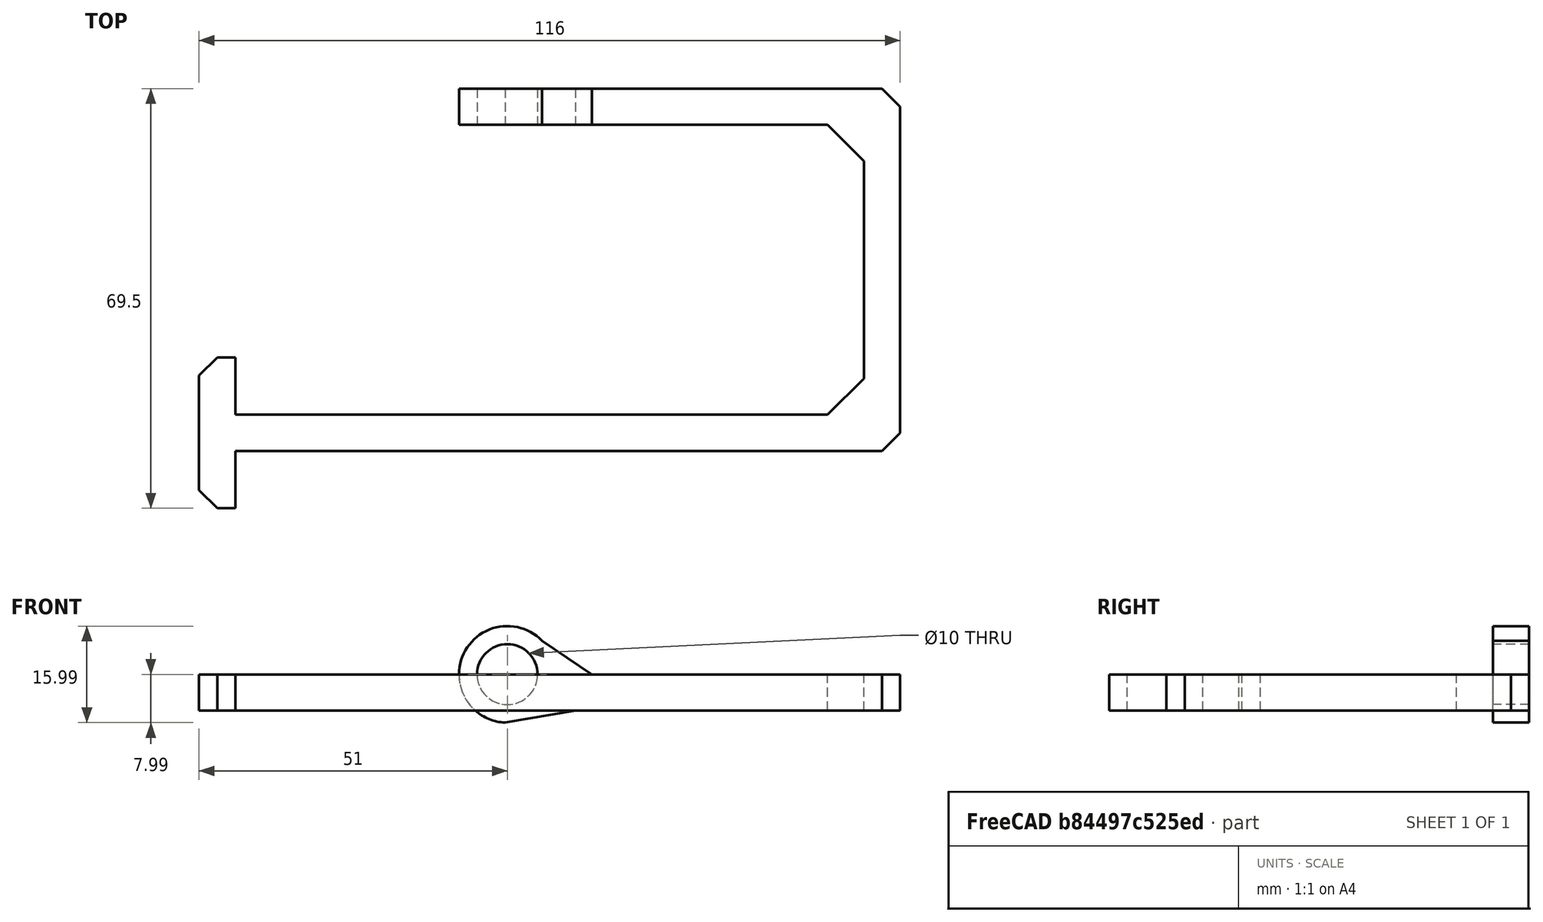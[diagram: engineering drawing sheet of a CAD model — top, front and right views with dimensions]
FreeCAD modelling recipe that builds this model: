
FCSTD DOCUMENT  (FreeCAD 0.19R24276 (Git))
Label: porta_rollos
License: All rights reserved
LicenseURL: http://en.wikipedia.org/wiki/All_rights_reserved
objects: TechDraw::DrawViewDimension×16, Part::Chamfer×8, TechDraw::DrawProjGroupItem×3, Part::Cylinder×2, TechDraw::DrawSVGTemplate×2, TechDraw::DrawViewPart×2, TechDraw::DrawPage×2, Sketcher::SketchObject×1, PartDesign::Pad×1, Part::Cut×1, Part::MultiFuse×1, TechDraw::DrawProjGroup×1, TechDraw::DrawViewAnnotation×1
note: 15 computed .brp shape members not serialized (recipe doc carries the construction recipe); baked Part::Feature solids carry a one-line shape summary decoded from their .brp

FEATURE [Sketcher::SketchObject] Sketch
  FullyConstrained = false
  MapMode = 5
  sketch-geometry (15):
    g0: LineSegment StartX=8 StartY=3 StartZ=0 EndX=68 EndY=3 EndZ=0
    g1: LineSegment StartX=68 StartY=3 StartZ=0 EndX=68 EndY=-57 EndZ=0
    g2: LineSegment StartX=68 StartY=-57 StartZ=0 EndX=-42 EndY=-57 EndZ=0
    g3: LineSegment StartX=-42 StartY=-51 StartZ=0 EndX=62 EndY=-51 EndZ=0
    g4: LineSegment StartX=62 StartY=-51 StartZ=0 EndX=62 EndY=-3 EndZ=0
    g5: LineSegment StartX=62 StartY=-3 StartZ=0 EndX=8 EndY=-3 EndZ=0
    g6: LineSegment StartX=8 StartY=3 StartZ=0 EndX=8 EndY=-3 EndZ=0
    g7: LineSegment StartX=62 StartY=-51 StartZ=0 EndX=68 EndY=-51 EndZ=0
    g8: LineSegment StartX=0 StartY=0 StartZ=0 EndX=8 EndY=0 EndZ=0
    g9: LineSegment StartX=-42 StartY=-51 StartZ=0 EndX=-42 EndY=-41.5 EndZ=0
    g10: LineSegment StartX=-42 StartY=-41.5 StartZ=0 EndX=-48 EndY=-41.5 EndZ=0
    g11: LineSegment StartX=-48 StartY=-41.5 StartZ=0 EndX=-48 EndY=-66.5 EndZ=0
    g12: LineSegment StartX=-48 StartY=-66.5 StartZ=0 EndX=-42 EndY=-66.5 EndZ=0
    g13: LineSegment StartX=-42 StartY=-66.5 StartZ=0 EndX=-42 EndY=-57 EndZ=0
    g14: LineSegment StartX=-42 StartY=-51 StartZ=0 EndX=-42 EndY=-57 EndZ=0
  constraints (43):
    c: Coincident(g1,g2)
    c: Coincident(g3,g4)
    c: Coincident(g4,g5)
    c: Vertical(g6)
    c: Horizontal(g0)
    c: Horizontal(g5)
    c: Horizontal(g3)
    c: Horizontal(g2)
    c: Vertical(g4)
    c: Vertical(g1)
    c: DistanceY(g6,g6) = 6
    c: Coincident(g1,g0)
    c: Horizontal(g7)
    c: Perpendicular(g7,g1) = 4.71239
    c: DistanceX(g7,g7) = 6
    c: DistanceX(g6,g0) = 60
    c: DistanceY(g1,g1) = 60
    c: DistanceX(g2,g2) = 110
    c: DistanceY(g2,g3) = 6
    c: Coincident(g7,g3)
    c: Coincident(g0,g6)
    c: Coincident(g5,g6)
    c: DistanceX(g8,g8) = 8
    c: Coincident(g8,g-1)
    c: Symmetric(g0,g5,g8)
    c: Perpendicular(g8,g6) = 4.71239
    c: Coincident(g9,g10)
    c: Coincident(g10,g11)
    c: Coincident(g11,g12)
    c: Coincident(g12,g13)
    c: Coincident(g13,g2)
    c: Coincident(g9,g3)
    c: Vertical(g9)
    c: Vertical(g13)
    c: Vertical(g11)
    c: Horizontal(g10)
    c: Horizontal(g12)
    c: Vertical(g14)
    c: Coincident(g14,g2)
    c: Coincident(g14,g3)
    c: DistanceX(g10,g10) = 6
    c: DistanceY(g11,g11) = 25
    c: DistanceY(g9,g9) = 9.5
FEATURE [PartDesign::Pad] Pad
  AllowMultiFace = false
  Direction = (1,1,1)
  Length = 6
  Length2 = 100
  Profile = -> Sketch
  Type = 0
FEATURE [Part::Cylinder] Cylinder  label="Cilindro"
  Angle = 360
  AttacherType = Attacher::AttachEngine3D
  Height = 6
  Placement = pos=(3,3,0) rot=(0,0,1;0rad)
  Radius = 8
FEATURE [Part::Cylinder] Cylinder001  label="Cilindro001"
  Angle = 360
  AttacherType = Attacher::AttachEngine3D
  Height = 6
  Placement = pos=(3,3,0) rot=(0,0,1;0rad)
  Radius = 5
FEATURE [Part::Cut] Cut
  Base = -> Cylinder
  Placement = pos=(0,3,3) rot=(1,0,0;1.5708rad)
  Tool = -> Cylinder001
FEATURE [Part::MultiFuse] Fusion
  Shapes = -> [Cut,Pad]
FEATURE [Part::Chamfer] Chamfer
  Base = -> Fusion
  Edges = 1 edges r=6: [Edge27]
FEATURE [Part::Chamfer] Chamfer001
  Base = -> Chamfer
  Edges = 1 edges r=6: [Edge41]
FEATURE [Part::Chamfer] Chamfer002
  Base = -> Chamfer001
  Edges = 1 edges r=6: [Edge40]
FEATURE [Part::Chamfer] Chamfer003
  Base = -> Chamfer002
  Edges = 1 edges r=6: [Edge15]
FEATURE [Part::Chamfer] Chamfer004
  Base = -> Chamfer003
  Edges = 1 edges r=3: [Edge36]
FEATURE [Part::Chamfer] Chamfer005
  Base = -> Chamfer004
  Edges = 1 edges r=3: [Edge26]
FEATURE [Part::Chamfer] Chamfer006
  Base = -> Chamfer005
  Edges = 1 edges r=3: [Edge35]
FEATURE [Part::Chamfer] Chamfer007
  Base = -> Chamfer006
  Edges = 1 edges r=3: [Edge25]
FEATURE [TechDraw::DrawSVGTemplate] Template
  EditableTexts = Designed_by_Name=<owner>; Drawing_number=001; FC-Date=-; FC-SC=1:3; FC-SH=1/2; FC-Title=Toilet Paper Holder; Subtitle=Porta Rollos Baño; Weight=<100gr
  Height = 210
  Orientation = 1
  Width = 297
FEATURE [TechDraw::DrawViewPart] View
  CoarseView = false
  Direction = (0.577,-0.577,0.577)
  Focus = 100
  HardHidden = false
  IsoCount = 0
  IsoHidden = false
  IsoVisible = false
  LockPosition = false
  Perspective = false
  Rotation = 0
  ScaleType = 0
  SeamHidden = false
  SeamVisible = true
  SmoothHidden = false
  SmoothVisible = true
  Source = -> [Chamfer007]
  X = 211.957
  XDirection = (0.707,0.707,0)
  Y = 129.533
FEATURE [TechDraw::DrawProjGroupItem] ProjItem  label="Front"
  CoarseView = false
  Direction = (0,-1,0)
  Focus = 100
  HardHidden = false
  IsoCount = 0
  IsoHidden = false
  IsoVisible = false
  LockPosition = true
  Perspective = false
  Rotation = 0
  RotationVector = (1,0,0)
  Scale = 0.5
  ScaleType = 2
  SeamHidden = false
  SeamVisible = true
  SmoothHidden = false
  SmoothVisible = true
  Source = -> [Chamfer007]
  Type = 0
  X = 0
  XDirection = (1,0,0)
  Y = 0
FEATURE [TechDraw::DrawProjGroupItem] ProjItem001  label="Right"
  CoarseView = false
  Direction = (1,-1e-16,0)
  Focus = 100
  HardHidden = false
  IsoCount = 0
  IsoHidden = false
  IsoVisible = false
  LockPosition = false
  Perspective = false
  Rotation = 0
  RotationVector = (1,0,0)
  ScaleType = 2
  SeamHidden = false
  SeamVisible = true
  SmoothHidden = false
  SmoothVisible = true
  Source = -> [Chamfer007]
  Type = 2
  X = -61.375
  XDirection = (1e-16,1,0)
  Y = 0
FEATURE [TechDraw::DrawProjGroupItem] ProjItem002  label="Top"
  CoarseView = false
  Direction = (0,0,1)
  Focus = 100
  HardHidden = false
  IsoCount = 0
  IsoHidden = false
  IsoVisible = false
  LockPosition = false
  Perspective = false
  Rotation = 0
  RotationVector = (1,0,0)
  ScaleType = 2
  SeamHidden = false
  SeamVisible = true
  SmoothHidden = false
  SmoothVisible = true
  Source = -> [Chamfer007]
  Type = 4
  X = 0
  XDirection = (1,0,0)
  Y = -49.75
FEATURE [TechDraw::DrawProjGroup] ProjGroup
  Anchor = -> ProjItem
  AutoDistribute = true
  LockPosition = false
  ProjectionType = 0
  Rotation = 0
  Scale = 0.5
  ScaleType = 2
  Source = -> [Chamfer007]
  Views = -> [ProjItem,ProjItem001,ProjItem002]
  X = 100.171
  Y = 156.257
  spacingX = 15
  spacingY = 15
FEATURE [TechDraw::DrawViewDimension] Dimension
  Arbitrary = false
  ArbitraryTolerances = false
  EqualTolerance = true
  FormatSpec = %.2f
  FormatSpecOverTolerance = %+.2f
  FormatSpecUnderTolerance = %+.2f
  Inverted = false
  LockPosition = false
  MeasureType = 1
  OverTolerance = 0
  References2D = -> [ProjItem002]
  Rotation = 0
  ScaleType = 0
  TheoreticalExact = false
  Type = 1
  UnderTolerance = 0
  X = -2.07471
  Y = 31.7463
FEATURE [TechDraw::DrawViewDimension] Dimension003
  Arbitrary = false
  ArbitraryTolerances = false
  EqualTolerance = true
  FormatSpec = %.2f
  FormatSpecOverTolerance = %+.2f
  FormatSpecUnderTolerance = %+.2f
  Inverted = false
  LockPosition = false
  MeasureType = 1
  OverTolerance = 0
  References2D = -> [ProjItem002]
  Rotation = 0
  ScaleType = 0
  TheoreticalExact = false
  Type = 2
  UnderTolerance = 0
  X = -47.3746
  Y = 3.19414
FEATURE [TechDraw::DrawPage] Page  label="Vistas"
  KeepUpdated = true
  NextBalloonIndex = 1
  ProjectionType = 0
  Template = -> Template
  Views = -> [View,ProjGroup,Dimension,Dimension003]
FEATURE [TechDraw::DrawSVGTemplate] Template001
  EditableTexts = Designed_by_Name=<owner>; Drawing_number=002; FC-Date=-; FC-SC=1:1; FC-SH=2/2; FC-Title=Toilet Paper Holder; Subtitle=Porta Rollos Baño; Weight=<100gr
  Height = 210
  Orientation = 1
  Width = 297
FEATURE [TechDraw::DrawViewPart] View001
  CoarseView = false
  Direction = (0.577,-0.577,0.577)
  Focus = 100
  HardHidden = false
  IsoCount = 0
  IsoHidden = false
  IsoVisible = false
  LockPosition = false
  Perspective = false
  Rotation = 0
  ScaleType = 0
  SeamHidden = false
  SeamVisible = true
  SmoothHidden = false
  SmoothVisible = true
  Source = -> [Chamfer007]
  X = 150.485
  XDirection = (0.707,0.707,0)
  Y = 127.165
FEATURE [TechDraw::DrawViewDimension] Dimension004
  Arbitrary = false
  ArbitraryTolerances = false
  EqualTolerance = true
  FormatSpec = %.2f
  FormatSpecOverTolerance = %+.2f
  FormatSpecUnderTolerance = %+.2f
  Inverted = false
  LockPosition = false
  MeasureType = 1
  OverTolerance = 0
  References2D = -> [View001]
  Rotation = 0
  ScaleType = 0
  TheoreticalExact = false
  Type = 0
  UnderTolerance = 0
  X = 47.6177
  Y = -19.1697
FEATURE [TechDraw::DrawViewDimension] Dimension005
  Arbitrary = false
  ArbitraryTolerances = false
  EqualTolerance = true
  FormatSpec = %.2f
  FormatSpecOverTolerance = %+.2f
  FormatSpecUnderTolerance = %+.2f
  Inverted = false
  LockPosition = false
  MeasureType = 1
  OverTolerance = 0
  References2D = -> [View001]
  Rotation = 0
  ScaleType = 0
  TheoreticalExact = false
  Type = 0
  UnderTolerance = 0
  X = 60.9185
  Y = -42.5373
FEATURE [TechDraw::DrawViewDimension] Dimension006
  Arbitrary = false
  ArbitraryTolerances = false
  EqualTolerance = true
  FormatSpec = %.2f
  FormatSpecOverTolerance = %+.2f
  FormatSpecUnderTolerance = %+.2f
  Inverted = false
  LockPosition = false
  MeasureType = 1
  OverTolerance = 0
  References2D = -> [View001]
  Rotation = 0
  ScaleType = 0
  TheoreticalExact = false
  Type = 0
  UnderTolerance = 0
  X = 22.8872
  Y = -5.37103
FEATURE [TechDraw::DrawViewDimension] Dimension007
  Arbitrary = false
  ArbitraryTolerances = false
  EqualTolerance = true
  FormatSpec = %.2f
  FormatSpecOverTolerance = %+.2f
  FormatSpecUnderTolerance = %+.2f
  Inverted = false
  LockPosition = false
  MeasureType = 1
  OverTolerance = 0
  References2D = -> [View001]
  Rotation = 0
  ScaleType = 0
  TheoreticalExact = false
  Type = 0
  UnderTolerance = 0
  X = 84.0256
  Y = -5.81118
FEATURE [TechDraw::DrawViewDimension] Dimension008
  Arbitrary = false
  ArbitraryTolerances = false
  EqualTolerance = true
  FormatSpec = %.2f
  FormatSpecOverTolerance = %+.2f
  FormatSpecUnderTolerance = %+.2f
  Inverted = false
  LockPosition = false
  MeasureType = 1
  OverTolerance = 0
  References2D = -> [View001]
  Rotation = 0
  ScaleType = 0
  TheoreticalExact = false
  Type = 0
  UnderTolerance = 0
  X = -19.77
  Y = -13.7624
FEATURE [TechDraw::DrawViewDimension] Dimension009
  Arbitrary = false
  ArbitraryTolerances = false
  EqualTolerance = true
  FormatSpec = %.2f
  FormatSpecOverTolerance = %+.2f
  FormatSpecUnderTolerance = %+.2f
  Inverted = false
  LockPosition = false
  MeasureType = 1
  OverTolerance = 0
  References2D = -> [View001]
  Rotation = 0
  ScaleType = 0
  TheoreticalExact = false
  Type = 0
  UnderTolerance = 0
  X = -83.7766
  Y = 11.8764
FEATURE [TechDraw::DrawViewDimension] Dimension010
  Arbitrary = false
  ArbitraryTolerances = false
  EqualTolerance = true
  FormatSpec = %.2f
  FormatSpecOverTolerance = %+.2f
  FormatSpecUnderTolerance = %+.2f
  Inverted = false
  LockPosition = false
  MeasureType = 1
  OverTolerance = 0
  References2D = -> [View001]
  Rotation = 0
  ScaleType = 0
  TheoreticalExact = false
  Type = 0
  UnderTolerance = 0
  X = -49.2593
  Y = 40.5521
FEATURE [TechDraw::DrawViewDimension] Dimension011
  Arbitrary = false
  ArbitraryTolerances = false
  EqualTolerance = true
  FormatSpec = %.2f
  FormatSpecOverTolerance = %+.2f
  FormatSpecUnderTolerance = %+.2f
  Inverted = false
  LockPosition = false
  MeasureType = 1
  OverTolerance = 0
  References2D = -> [View001]
  Rotation = 0
  ScaleType = 0
  TheoreticalExact = false
  Type = 0
  UnderTolerance = 0
  X = -29.1655
  Y = 25.4834
FEATURE [TechDraw::DrawViewDimension] Dimension012
  Arbitrary = false
  ArbitraryTolerances = false
  EqualTolerance = true
  FormatSpec = %.2f
  FormatSpecOverTolerance = %+.2f
  FormatSpecUnderTolerance = %+.2f
  Inverted = false
  LockPosition = false
  MeasureType = 1
  OverTolerance = 0
  References2D = -> [View001]
  Rotation = 0
  ScaleType = 0
  TheoreticalExact = false
  Type = 0
  UnderTolerance = 0
  X = -84.8838
  Y = 32.6153
FEATURE [TechDraw::DrawViewDimension] Dimension013
  Arbitrary = false
  ArbitraryTolerances = false
  EqualTolerance = true
  FormatSpec = %.2f
  FormatSpecOverTolerance = %+.2f
  FormatSpecUnderTolerance = %+.2f
  Inverted = false
  LockPosition = false
  MeasureType = 1
  OverTolerance = 0
  References2D = -> [View001]
  Rotation = 0
  ScaleType = 0
  TheoreticalExact = false
  Type = 0
  UnderTolerance = 0
  X = 51.633
  Y = 23.3392
FEATURE [TechDraw::DrawViewDimension] Dimension015
  Arbitrary = false
  ArbitraryTolerances = false
  EqualTolerance = true
  FormatSpec = R%.2f
  FormatSpecOverTolerance = %+.2f
  FormatSpecUnderTolerance = %+.2f
  Inverted = false
  LockPosition = false
  MeasureType = 1
  OverTolerance = 0
  References2D = -> [View001]
  Rotation = 0
  ScaleType = 0
  TheoreticalExact = false
  Type = 4
  UnderTolerance = 0
  X = 24.9015
  Y = 44.0024
FEATURE [TechDraw::DrawViewDimension] Dimension017
  Arbitrary = false
  ArbitraryTolerances = false
  EqualTolerance = true
  FormatSpec = %.2f
  FormatSpecOverTolerance = %+.2f
  FormatSpecUnderTolerance = %+.2f
  Inverted = false
  LockPosition = false
  MeasureType = 1
  OverTolerance = 0
  References2D = -> [View001]
  Rotation = 0
  ScaleType = 0
  TheoreticalExact = false
  Type = 0
  UnderTolerance = 0
  X = -6.81241
  Y = 35.2351
FEATURE [TechDraw::DrawViewDimension] Dimension018
  Arbitrary = false
  ArbitraryTolerances = false
  EqualTolerance = true
  FormatSpec = %.2f
  FormatSpecOverTolerance = %+.2f
  FormatSpecUnderTolerance = %+.2f
  Inverted = false
  LockPosition = false
  MeasureType = 1
  OverTolerance = 0
  References2D = -> [View001]
  Rotation = 0
  ScaleType = 0
  TheoreticalExact = false
  Type = 2
  UnderTolerance = 0
  X = -34.7076
  Y = -27.0109
FEATURE [TechDraw::DrawViewAnnotation] Annotation
  Font = osifont
  LineSpace = 80
  LockPosition = false
  MaxWidth = -1
  Rotation = 0
  ScaleType = 0
  Text = Aproximate measurements: | Check with 3D piece
  TextSize = 5
  TextStyle = 0
  X = 76.3713
  Y = 68.7223
FEATURE [TechDraw::DrawViewDimension] Dimension019
  Arbitrary = false
  ArbitraryTolerances = false
  EqualTolerance = true
  FormatSpec = %.2f
  FormatSpecOverTolerance = %+.2f
  FormatSpecUnderTolerance = %+.2f
  Inverted = false
  LockPosition = false
  MeasureType = 1
  OverTolerance = 0
  References2D = -> [View001]
  Rotation = 0
  ScaleType = 0
  TheoreticalExact = false
  Type = 0
  UnderTolerance = 0
  X = 14.8451
  Y = 8.11632
FEATURE [TechDraw::DrawPage] Page001  label="Cotas"
  KeepUpdated = true
  NextBalloonIndex = 1
  ProjectionType = 0
  Template = -> Template001
  Views = -> [View001,Dimension004,Dimension005,Dimension006,Dimension007,Dimension008,Dimension009,Dimension010,Dimension011,Dimension012,Dimension013,Dimension015,Dimension017,Dimension018,Annotation,Dimension019]
